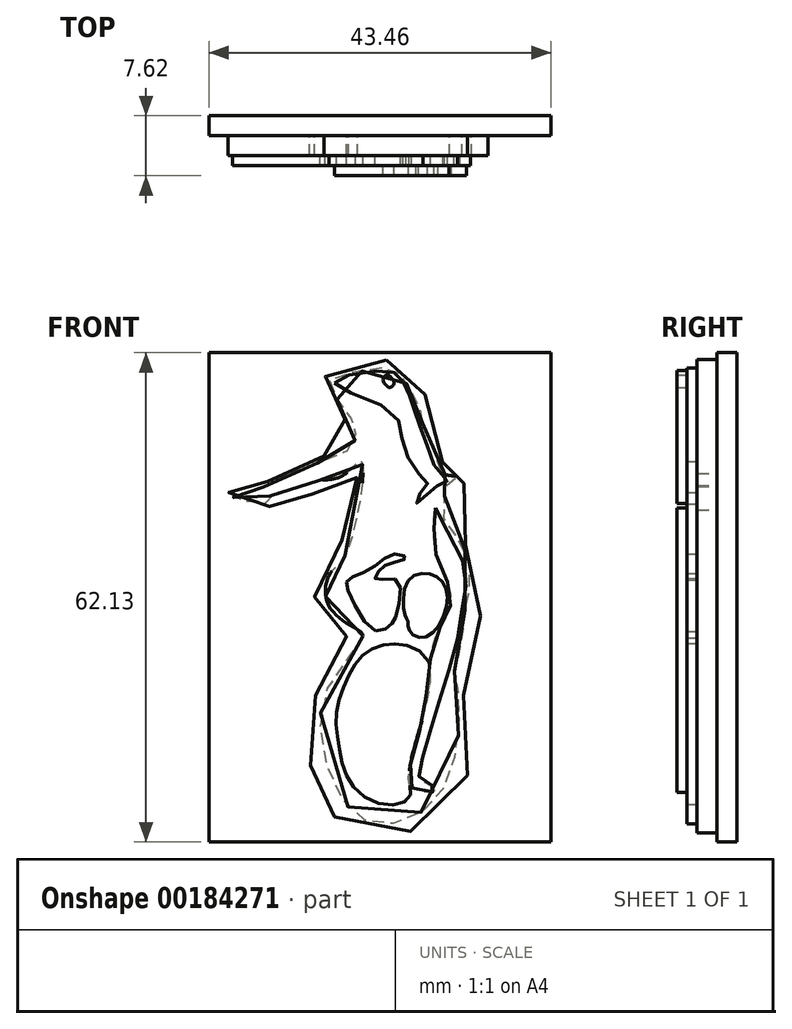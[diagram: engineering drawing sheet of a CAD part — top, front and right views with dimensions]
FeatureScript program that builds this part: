
annotation { "Feature Type Name" : "Feature", "Feature Type Description" : "" }
export const myFeature = defineFeature(function(context is Context, id is Id, definition is map)
    precondition{}
    {
        {
            var Q0;
            Q0=qCreatedBy(makeId("Front.planeOp"),FACE);
            var sketch = newSketch(context, id + "F0", { "sketchPlane" : qUnion([Q0])});
            skLineSegment(sketch, "E0.bottom", {"start": v(-22.55, 45.7) * mm, "end": v(20.91, 45.7) * mm});
            skLineSegment(sketch, "E0.top", {"start": v(-22.55, -16.43) * mm, "end": v(20.91, -16.43) * mm});
            skLineSegment(sketch, "E0.left", {"start": v(-22.55, 45.7) * mm, "end": v(-22.55, -16.43) * mm});
            skLineSegment(sketch, "E0.right", {"start": v(20.91, 45.7) * mm, "end": v(20.91, -16.43) * mm});
            skSolve(sketch);
        }
        {
            var Q0;
            Q0 = qSketchRegion(id + "F0", true);
            extrude(context, id + "F1", {"entities" : qUnion([Q0]), "oppositeDirection" : true, "depth" : 2.54 * mm});
        }
        {
            var Q0;
            Q0=makeQuery(id+"F1.opExtrude","CAP_FACE",FACE,{"disambiguationData":[OSD([sQuery(id+"F0.wireOp",EDGE,"E0.bottom"),sQuery(id+"F0.wireOp",EDGE,"E0.top"),sQuery(id+"F0.wireOp",EDGE,"E0.left"),sQuery(id+"F0.wireOp",EDGE,"E0.right")])],"isStart":true});
            var sketch = newSketch(context, id + "F2", { "sketchPlane" : qUnion([Q0])});
            skFitSpline(sketch, "E1", {"points": [v(0, 44.8) * mm, v(-7.35, 43.23) * mm, v(-7.49, 40.31) * mm, v(-5, 36.6) * mm, v(-5.92, 33.47) * mm, v(-12.12, 31.33) * mm, v(-16.47, 28.76) * mm, v(-19.47, 28.69) * mm, v(-19.82, 26.62) * mm, v(-14.9, 26.12) * mm, v(-14.33, 27.26) * mm, v(-7.84, 28.12) * mm, v(-4.07, 30.33) * mm, v(-4.28, 25.12) * mm, v(-7.42, 19) * mm, v(-8.84, 13.36) * mm, v(-5.14, 10.08) * mm, v(-8.06, 4.52) * mm, v(-9.77, -3.96) * mm, v(-8.77, -10.45) * mm, v(-4.7, -14.3) * mm, v(6.34, -13.87) * mm, v(10.76, -3.46) * mm, v(9.7, 6.16) * mm, v(12.69, 17.43) * mm, v(7.98, 24.91) * mm, v(10.26, 30.26) * mm, v(7.7, 30.83) * mm, v(6.77, 35.89) * mm, v(2.56, 43.52) * mm, v(0, 44.8) * mm]});
            skSolve(sketch);
        }
        {
            var Q0;
            Q0 = qSketchRegion(id + "F2", true);
            extrude(context, id + "F3", {"entities" : qUnion([Q0]), "operationType" : NewBodyOperationType.ADD, "depth" : 2.54 * mm});
        }
        {
            var Q0;
            Q0=makeQuery(id+"F3.opExtrude","CAP_FACE",FACE,{"disambiguationData":[OSD([sQuery(id+"F2.wireOp",EDGE,"E1")])],"isStart":false});
            var sketch = newSketch(context, id + "F4", { "sketchPlane" : qUnion([Q0])});
            skFitSpline(sketch, "E2", {"points": [v(-3, 9.72) * mm, v(-7.41, 3.36) * mm, v(-7.07, -8.25) * mm, v(-1.99, -13.93) * mm, v(4.88, -12.32) * mm, v(8.7, -5.54) * mm, v(9.03, 3.3) * mm, v(8.55, 4.85) * mm, v(9.46, 8.37) * mm, v(9.94, 12.91) * mm, v(10.42, 15) * mm, v(10.05, 20.55) * mm, v(7.27, 24.72) * mm, v(7.38, 27.6) * mm, v(7.38, 28.67) * mm, v(9.03, 29.9) * mm, v(7.32, 30.27) * mm, v(6.42, 32.25) * mm, v(4.6, 36.73) * mm, v(4.6, 37.59) * mm, v(3.53, 40.05) * mm, v(2.36, 42.08) * mm, v(1.02, 43.57) * mm, v(-2.45, 43.52) * mm, v(-7.1, 42.34) * mm, v(-7.2, 41.38) * mm, v(-4.85, 37.75) * mm, v(-4.21, 36.9) * mm, v(-4, 34.65) * mm, v(-5.28, 33.05) * mm, v(-7.04, 32.36) * mm, v(-10.35, 31.07) * mm, v(-14.47, 29.36) * mm, v(-16.28, 28.3) * mm, v(-17.78, 27.98) * mm, v(-19.43, 27.82) * mm, v(-19.49, 27.33) * mm, v(-17.94, 26.85) * mm, v(-15.38, 26.64) * mm, v(-14.63, 27.7) * mm, v(-12.54, 28.19) * mm, v(-8.8, 29.42) * mm, v(-5.44, 30.17) * mm, v(-3.25, 31.87) * mm, v(-4.32, 22.58) * mm, v(-6.08, 18.79) * mm, v(-7.2, 17.61) * mm, v(-7.63, 14.25) * mm, v(-4.7, 11.1) * mm, v(-3, 9.72) * mm]});
            skFitSpline(sketch, "E3", {"points": [v(-1.38, 10.37) * mm, v(-4.94, 15.63) * mm, v(-4.88, 16.9) * mm, v(-1.89, 18.3) * mm, v(0.9, 20.14) * mm, v(2.5, 19.63) * mm, v(0.65, 19) * mm, v(-0.94, 18.04) * mm, v(-1.38, 16.9) * mm, v(1.35, 16.83) * mm, v(1.16, 12.26) * mm, v(0.59, 11.18) * mm, v(-1.38, 10.37) * mm]});
            skFitSpline(sketch, "E4", {"points": [v(5.03, 9.6) * mm, v(7.7, 14.1) * mm, v(6.3, 17.28) * mm, v(2.87, 16.9) * mm, v(2.3, 12.45) * mm, v(2.69, 11.62) * mm, v(2.9, 10.37) * mm, v(5.03, 9.6) * mm]});
            skFitSpline(sketch, "E5", {"points": [v(5.31, 6.51) * mm, v(2.63, 8.48) * mm, v(0, 8.64) * mm, v(-2.4, 7.75) * mm, v(-4.1, 5.95) * mm, v(-5.5, 3.14) * mm, v(-6.39, 0) * mm, v(-6.3, -2.63) * mm, v(-5.75, -5.91) * mm, v(-4.58, -8.94) * mm, v(-1.37, -11.45) * mm, v(2.07, -11.46) * mm, v(3.06, -10.28) * mm, v(2.87, -8.21) * mm, v(4.28, -1.76) * mm, v(5.31, 6.51) * mm]});
            skSolve(sketch);
        }
        {
            var Q0;
            Q0 = qSketchRegion(id + "F4", true);
            extrude(context, id + "F5", {"entities" : qUnion([Q0]), "operationType" : NewBodyOperationType.ADD, "depth" : 1.27 * mm});
        }
        {
            var Q0;
            Q0=makeQuery(id+"F5.opExtrude","CAP_FACE",FACE,{"disambiguationData":[OSD([sQuery(id+"F4.wireOp",EDGE,"E2"),sQuery(id+"F4.wireOp",EDGE,"E3"),sQuery(id+"F4.wireOp",EDGE,"E4")])],"isStart":false});
            var sketch = newSketch(context, id + "F6", { "sketchPlane" : qUnion([Q0])});
            skFitSpline(sketch, "E6", {"points": [v(-6.64, 41.84) * mm, v(0.56, 38.28) * mm, v(1.98, 34.5) * mm, v(4.05, 30.36) * mm, v(5.2, 28.94) * mm, v(3.84, 27.3) * mm, v(3.9, 26.59) * mm, v(5.83, 28.44) * mm, v(6.83, 28.9) * mm, v(7.9, 29.68) * mm, v(7, 30.08) * mm, v(5.1, 33.98) * mm, v(3.73, 37.79) * mm, v(2.75, 40.61) * mm, v(1.5, 42.83) * mm, v(-1.12, 43.4) * mm, v(-6.64, 41.84) * mm]});
            skFitSpline(sketch, "E7", {"points": [v(0, 42.87) * mm, v(0.6, 42.56) * mm, v(0.94, 41.84) * mm, v(0.47, 41.29) * mm, v(0, 41.52) * mm, v(-0.44, 42.26) * mm, v(0, 42.87) * mm]});
            skFitSpline(sketch, "E8", {"points": [v(6.2, 26) * mm, v(8.28, 21.92) * mm, v(10.14, 17.8) * mm, v(9.65, 13.73) * mm, v(9.16, 9.98) * mm, v(7.65, 4.53) * mm, v(5.87, -1.13) * mm, v(4.69, -5.36) * mm, v(4.1, -7.66) * mm, v(4.36, -8.62) * mm, v(6.07, -9.43) * mm, v(6.5, -9.86) * mm, v(4.62, -10.12) * mm, v(2.91, -9.1) * mm, v(3.62, -4.6) * mm, v(5.03, 2.13) * mm, v(6.22, 9.52) * mm, v(7.94, 13.04) * mm, v(8.05, 15.72) * mm, v(6.3, 20.06) * mm, v(6.04, 23.91) * mm, v(6.2, 26) * mm]});
            skSolve(sketch);
        }
        {
            var Q0;
            Q0 = qSketchRegion(id + "F6", true);
            extrude(context, id + "F7", {"entities" : qUnion([Q0]), "operationType" : NewBodyOperationType.ADD, "depth" : 1.27 * mm});
        }
    });
